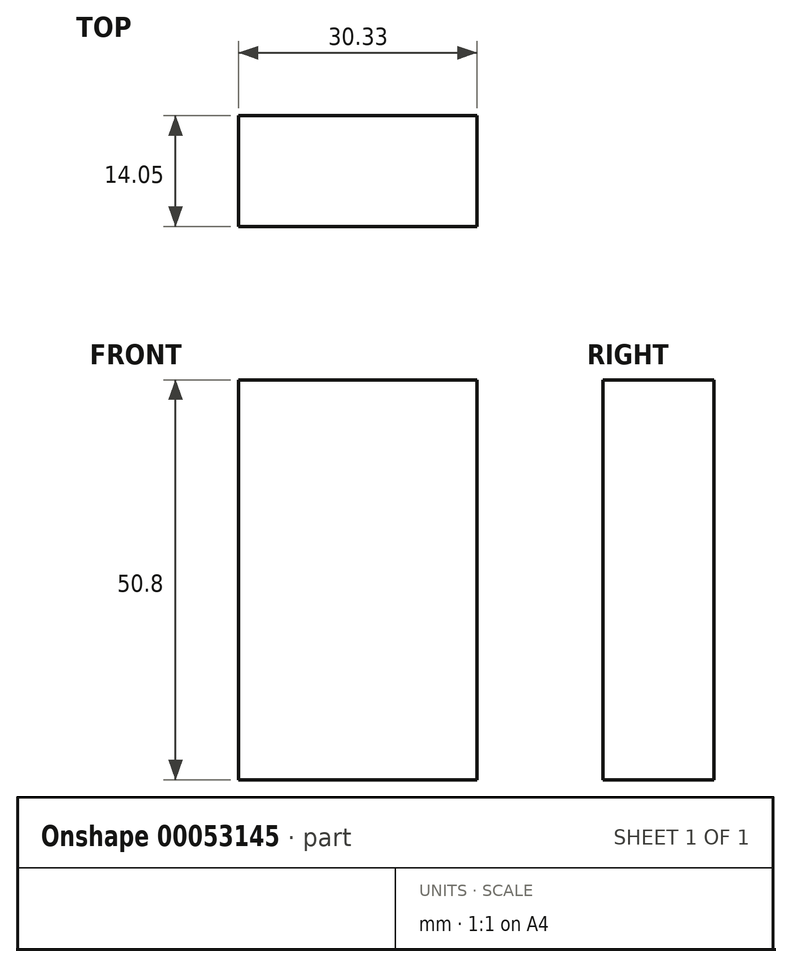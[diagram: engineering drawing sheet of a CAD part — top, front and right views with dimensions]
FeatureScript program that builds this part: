
annotation { "Feature Type Name" : "Feature", "Feature Type Description" : "" }
export const myFeature = defineFeature(function(context is Context, id is Id, definition is map)
    precondition{}
    {
        {
            var Q0;
            Q0=qCreatedBy(makeId("Top.planeOp"),FACE);
            var sketch = newSketch(context, id + "F0", { "sketchPlane" : qUnion([Q0])});
            skArc(sketch, "E0", {"start": v(-25.89, 16.64) * mm, "mid": v(-26.95, 42.4) * mm, "end": v(-52.27, 47.22) * mm});
            skLineSegment(sketch, "E1.bottom", {"start": v(-63.12, 17.63) * mm, "end": v(-32.8, 17.63) * mm});
            skLineSegment(sketch, "E1.top", {"start": v(-63.12, 3.58) * mm, "end": v(-32.8, 3.58) * mm});
            skLineSegment(sketch, "E1.left", {"start": v(-63.12, 17.63) * mm, "end": v(-63.12, 3.58) * mm});
            skLineSegment(sketch, "E1.right", {"start": v(-32.8, 17.63) * mm, "end": v(-32.8, 3.58) * mm});
            skSolve(sketch);
        }
        {
            var Q0;
            Q0=makeQuery(id+"F0.imprint","IMPRINT",FACE,{"disambiguationData":[TD([[makeQuery(id+"F0.imprint","IMPRINT",EDGE,{"derivedFrom":sQuery(id+"F0.wireOp",EDGE,"E1.bottom")}),-1.0]])]});
            extrude(context, id + "F1", {"entities" : qUnion([Q0]), "depth" : 50.8 * mm});
        }
    });
